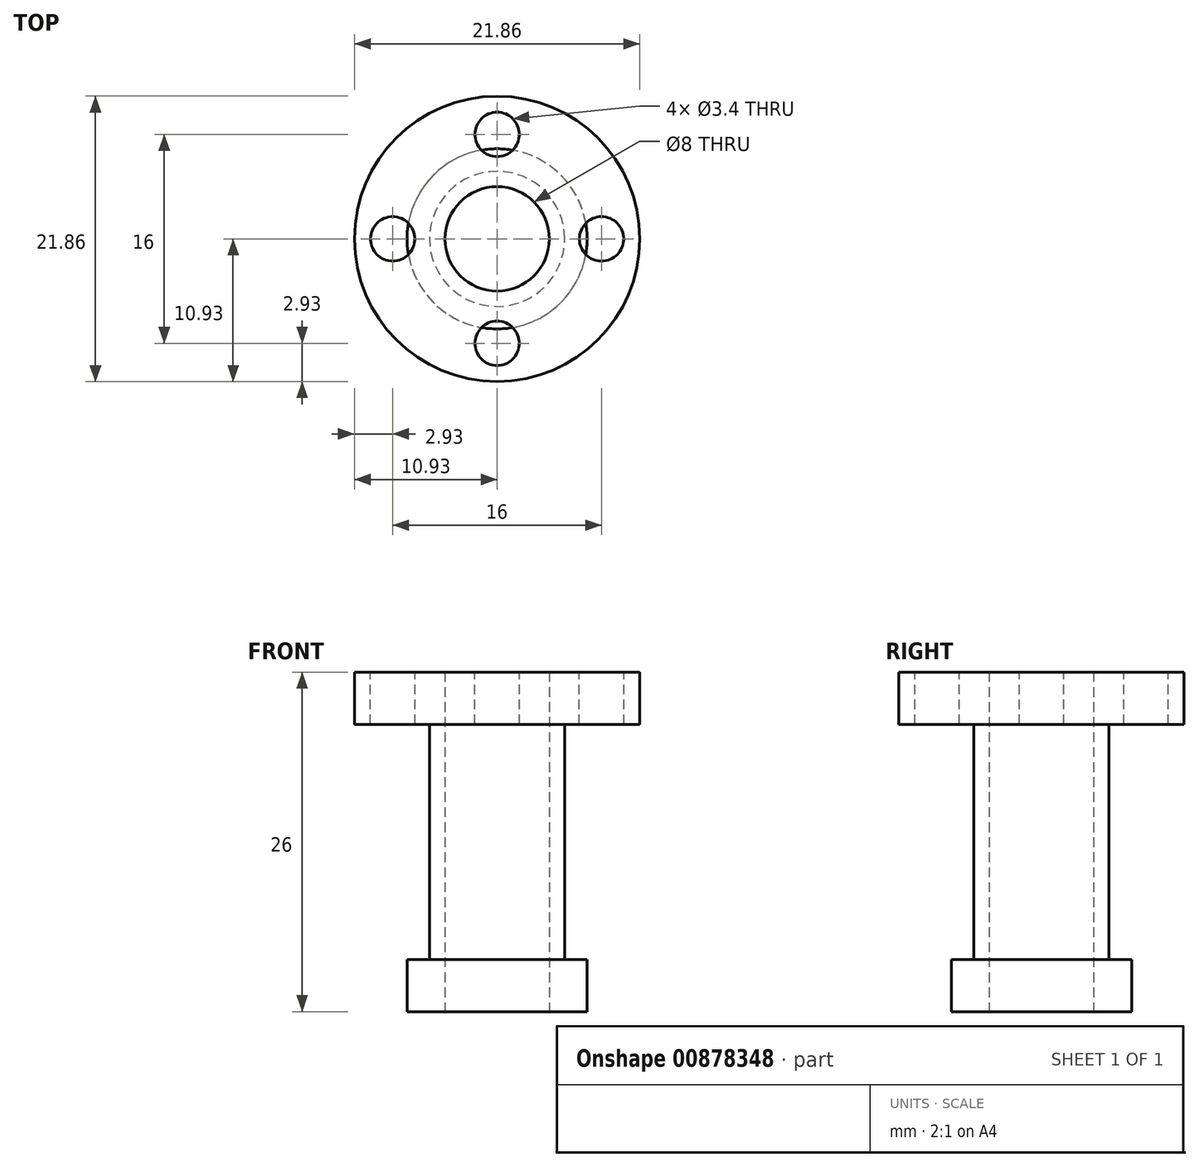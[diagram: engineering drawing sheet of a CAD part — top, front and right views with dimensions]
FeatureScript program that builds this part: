
annotation { "Feature Type Name" : "Feature", "Feature Type Description" : "" }
export const myFeature = defineFeature(function(context is Context, id is Id, definition is map)
    precondition{}
    {
        {
            var Q0;
            Q0=qCreatedBy(makeId("Top.planeOp"),FACE);
            var sketch = newSketch(context, id + "F0", { "sketchPlane" : qUnion([Q0])});
            skCircle(sketch, "E0", {"center": v(0, 0) * mm, "radius": 10.93 * mm});
            skCircle(sketch, "E1", {"center": v(0, 0) * mm, "radius": 4 * mm});
            skSolve(sketch);
        }
        {
            var Q0;
            Q0=makeQuery(id+"F0.imprint","IMPRINT",FACE,{"disambiguationData":[TD([[makeQuery(id+"F0.imprint","IMPRINT",EDGE,{"derivedFrom":sQuery(id+"F0.wireOp",EDGE,"E0")}),1.0]])]});
            extrude(context, id + "F1", {"entities" : qUnion([Q0]), "depth" : 4 * mm, "offsetDistance" : 25 * mm});
        }
        {
            var Q0;
            Q0=makeQuery(id+"F1.opExtrude","CAP_FACE",FACE,{"disambiguationData":[OSD([sQuery(id+"F0.wireOp",EDGE,"E0"),sQuery(id+"F0.wireOp",EDGE,"E1")])],"isStart":false});
            var sketch = newSketch(context, id + "F2", { "sketchPlane" : qUnion([Q0])});
            skCircle(sketch, "E2", {"center": v(8, 0) * mm, "radius": 1.7 * mm});
            skCircle(sketch, "E3", {"center": v(-8, 0) * mm, "radius": 1.7 * mm});
            skCircle(sketch, "E4", {"center": v(0, 8) * mm, "radius": 1.7 * mm});
            skCircle(sketch, "E5", {"center": v(0, -8) * mm, "radius": 1.7 * mm});
            skSolve(sketch);
        }
        {
            var Q0;
            Q0=makeQuery(id+"F2.imprint","IMPRINT",FACE,{"disambiguationData":[TD([[makeQuery(id+"F2.imprint","IMPRINT",EDGE,{"derivedFrom":sQuery(id+"F2.wireOp",EDGE,"E4")}),1.0]])]});
            var Q1;
            Q1=makeQuery(id+"F2.imprint","IMPRINT",FACE,{"disambiguationData":[TD([[makeQuery(id+"F2.imprint","IMPRINT",EDGE,{"derivedFrom":sQuery(id+"F2.wireOp",EDGE,"E3")}),1.0]])]});
            var Q2;
            Q2=makeQuery(id+"F2.imprint","IMPRINT",FACE,{"disambiguationData":[TD([[makeQuery(id+"F2.imprint","IMPRINT",EDGE,{"derivedFrom":sQuery(id+"F2.wireOp",EDGE,"E2")}),1.0]])]});
            var Q3;
            Q3=makeQuery(id+"F2.imprint","IMPRINT",FACE,{"disambiguationData":[TD([[makeQuery(id+"F2.imprint","IMPRINT",EDGE,{"derivedFrom":sQuery(id+"F2.wireOp",EDGE,"E5")}),1.0]])]});
            var Q4;
            Q4=makeQuery(id+"F1.opExtrude","CAP_FACE",FACE,{"disambiguationData":[OSD([sQuery(id+"F0.wireOp",EDGE,"E0"),sQuery(id+"F0.wireOp",EDGE,"E1")])],"isStart":true});
            extrude(context, id + "F3", {"entities" : qUnion([Q0, Q1, Q2, Q3]), "operationType" : NewBodyOperationType.REMOVE, "endBound" : BoundingType.UP_TO_SURFACE, "oppositeDirection" : true, "depth" : 25 * mm, "endBoundEntityFace" : qUnion([Q4]), "offsetDistance" : 25 * mm});
        }
        {
            var Q0;
            Q0=makeQuery(id+"F1.opExtrude","CAP_FACE",FACE,{"disambiguationData":[OSD([sQuery(id+"F0.wireOp",EDGE,"E0"),sQuery(id+"F0.wireOp",EDGE,"E1")])],"isStart":true});
            var sketch = newSketch(context, id + "F4", { "sketchPlane" : qUnion([Q0])});
            skCircle(sketch, "E6", {"center": v(0, 0) * mm, "radius": 5.17 * mm});
            skSolve(sketch);
        }
        {
            var Q0;
            Q0=makeQuery(id+"F4.imprint","IMPRINT",FACE,{"disambiguationData":[TD([[makeQuery(id+"F4.imprint","IMPRINT",EDGE,{"derivedFrom":sQuery(id+"F4.wireOp",EDGE,"E6")}),1.0]])]});
            extrude(context, id + "F5", {"entities" : qUnion([Q0]), "operationType" : NewBodyOperationType.ADD, "depth" : 11 * mm, "offsetDistance" : 25 * mm});
        }
        {
            var Q0;
            Q0=makeQuery(id+"F5.opExtrude","CAP_FACE",FACE,{"disambiguationData":[OSD([sQuery(id+"F0.wireOp",EDGE,"E1"),sQuery(id+"F4.wireOp",EDGE,"E6")])],"isStart":false});
            extrude(context, id + "F6", {"entities" : qUnion([Q0]), "operationType" : NewBodyOperationType.ADD, "depth" : 11 * mm, "offsetDistance" : 25 * mm});
        }
        {
            var Q0;
            Q0=makeQuery(id+"F6.opExtrude","CAP_FACE",FACE,{"disambiguationData":[OSD([sQuery(id+"F0.wireOp",EDGE,"E1"),sQuery(id+"F4.wireOp",EDGE,"E6")])],"isStart":false});
            var sketch = newSketch(context, id + "F7", { "sketchPlane" : qUnion([Q0])});
            skCircle(sketch, "E7", {"center": v(0, 0) * mm, "radius": 6.9 * mm});
            skSolve(sketch);
        }
        {
            var Q0;
            Q0=makeQuery(id+"F7.imprint","IMPRINT",FACE,{"disambiguationData":[TD([[makeQuery(id+"F7.imprint","IMPRINT",EDGE,{"derivedFrom":sQuery(id+"F7.wireOp",EDGE,"E7")}),1.0]])]});
            extrude(context, id + "F8", {"entities" : qUnion([Q0]), "operationType" : NewBodyOperationType.ADD, "oppositeDirection" : true, "depth" : 4 * mm, "offsetDistance" : 25 * mm});
        }
    });
